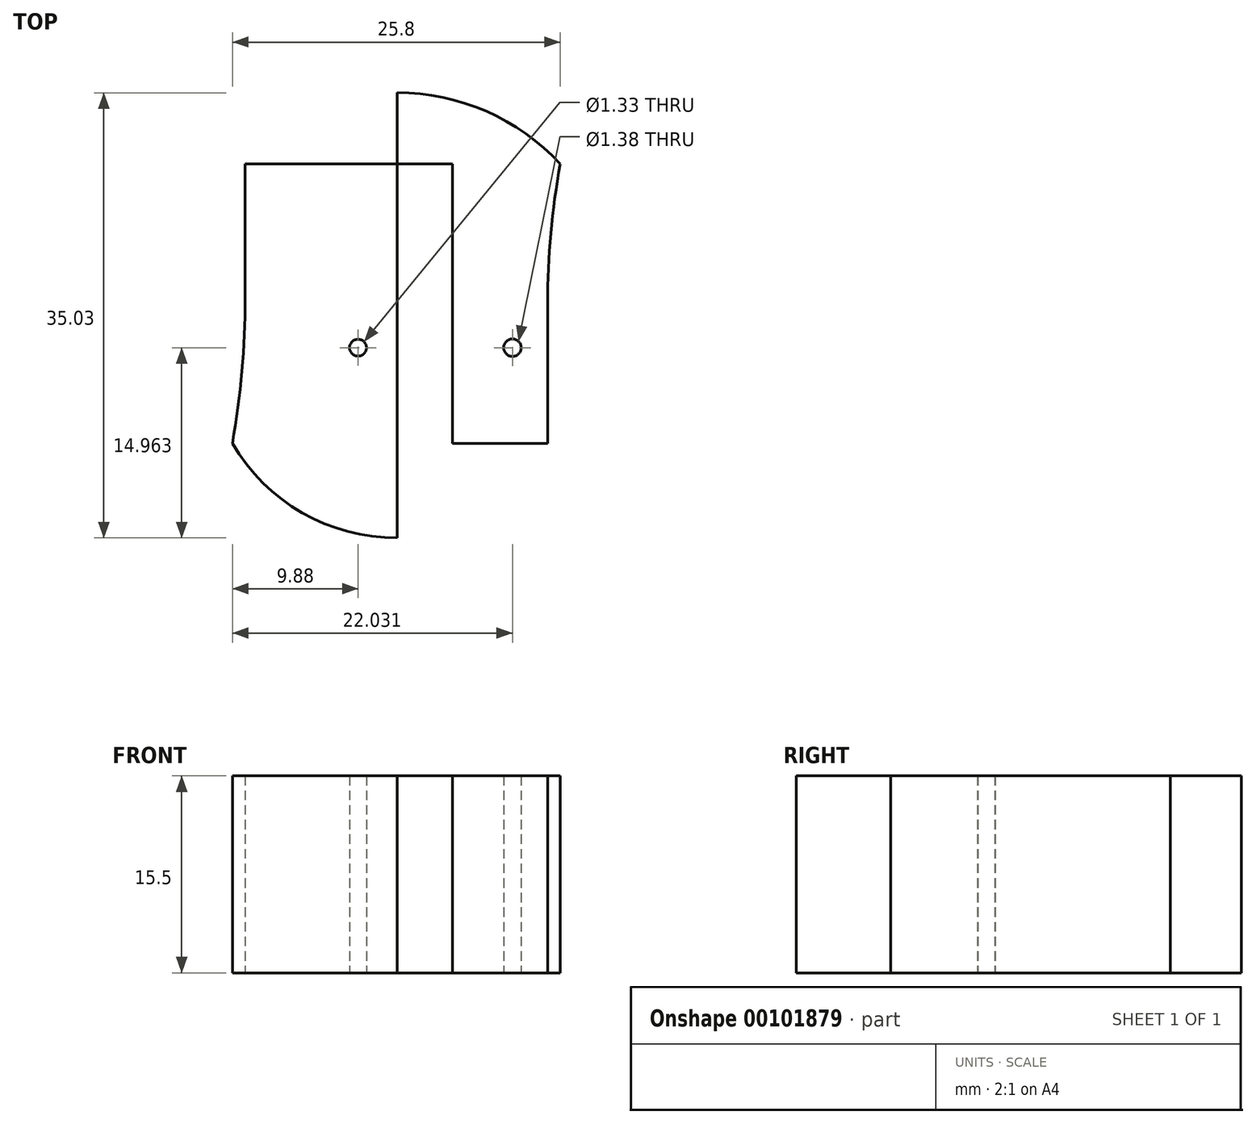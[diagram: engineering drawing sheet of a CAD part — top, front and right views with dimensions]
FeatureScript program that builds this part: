
annotation { "Feature Type Name" : "Feature", "Feature Type Description" : "" }
export const myFeature = defineFeature(function(context is Context, id is Id, definition is map)
    precondition{}
    {
        {
            var Q0;
            Q0=qCreatedBy(makeId("Top.planeOp"),FACE);
            var sketch = newSketch(context, id + "F0", { "sketchPlane" : qUnion([Q0])});
            skLineSegment(sketch, "E0.bottom", {"start": v(-29.3, -33.43) * mm, "end": v(-5.5, -33.43) * mm});
            skLineSegment(sketch, "E0.top", {"start": v(-29.3, -55.43) * mm, "end": v(-5.5, -55.43) * mm});
            skLineSegment(sketch, "E0.left", {"start": v(-29.3, -33.43) * mm, "end": v(-29.3, -55.43) * mm});
            skLineSegment(sketch, "E0.right", {"start": v(-5.5, -33.43) * mm, "end": v(-5.5, -55.43) * mm});
            skLineSegment(sketch, "E1", {"start": v(-26.8, -33.43) * mm, "end": v(-26.8, -55.43) * mm});
            skLineSegment(sketch, "E2", {"start": v(-7, -33.43) * mm, "end": v(-7, -55.43) * mm});
            skLineSegment(sketch, "E3", {"start": v(-17.4, -33.43) * mm, "end": v(-17.4, -46.37) * mm});
            skLineSegment(sketch, "E4", {"start": v(-17.4, -46.37) * mm, "end": v(-14.51, -46.37) * mm});
            skLineSegment(sketch, "E5", {"start": v(-14.51, -46.37) * mm, "end": v(-14.51, -55.43) * mm});
            skLineSegment(sketch, "E6", {"start": v(-18.41, -33.43) * mm, "end": v(-18.41, -55.43) * mm});
            skCircle(sketch, "E7", {"center": v(-20.42, -47.9) * mm, "radius": 0.66 * mm});
            skCircle(sketch, "E8", {"center": v(-8.27, -47.9) * mm, "radius": 0.69 * mm});
            skLineSegment(sketch, "E9", {"start": v(-12.98, -55.43) * mm, "end": v(-12.98, -33.43) * mm});
            skArc(sketch, "E10", {"start": v(-30.3, -55.43) * mm, "mid": v(-17.4, -62.86) * mm, "end": v(-4.5, -55.43) * mm});
            skArc(sketch, "E11", {"start": v(-4.5, -33.43) * mm, "mid": v(-17.33, -27.83) * mm, "end": v(-30.17, -33.43) * mm});
            skArc(sketch, "E12", {"start": v(-30.3, -55.43) * mm, "mid": v(-29.3, -44.43) * mm, "end": v(-30.17, -33.43) * mm});
            skArc(sketch, "E13", {"start": v(-4.5, -33.43) * mm, "mid": v(-5.5, -44.43) * mm, "end": v(-4.5, -55.43) * mm});
            skLineSegment(sketch, "E14", {"start": v(-17.33, -27.83) * mm, "end": v(-17.33, -62.86) * mm});
            skSolve(sketch);
        }
        {
            var Q0;
            {var subQ1=sQuery(id+"F0.wireOp",EDGE,"E10");Q0=makeQuery(id+"F0.imprint","IMPRINT",FACE,{"disambiguationData":[TD([[makeQuery(id+"F0.imprint","IMPRINT",EDGE,{"derivedFrom":subQ1}),1.0]])]});}
            var Q1;
            {var subQ0=sQuery(id+"F0.wireOp",EDGE,"E11");Q1=makeQuery(id+"F0.imprint","IMPRINT",FACE,{"disambiguationData":[TD([[makeQuery(id+"F0.imprint","IMPRINT",EDGE,{"derivedFrom":subQ0}),1.0]])]});}
            var Q2;
            {var subQ4=sQuery(id+"F0.wireOp",EDGE,"E1");Q2=makeQuery(id+"F0.imprint","IMPRINT",FACE,{"disambiguationData":[TD([[makeQuery(id+"F0.imprint","IMPRINT",EDGE,{"derivedFrom":subQ4}),-1.0]])]});}
            var Q3;
            {var subQ1=sQuery(id+"F0.wireOp",EDGE,"E1");Q3=makeQuery(id+"F0.imprint","IMPRINT",FACE,{"disambiguationData":[TD([[makeQuery(id+"F0.imprint","IMPRINT",EDGE,{"derivedFrom":subQ1}),1.0]])]});}
            var Q4;
            {var subQ3=sQuery(id+"F0.wireOp",EDGE,"E3");Q4=makeQuery(id+"F0.imprint","IMPRINT",FACE,{"disambiguationData":[TD([[makeQuery(id+"F0.imprint","IMPRINT",EDGE,{"derivedFrom":subQ3}),-1.0]])]});}
            var Q5;
            {var subQ3=sQuery(id+"F0.wireOp",EDGE,"E3");Q5=makeQuery(id+"F0.imprint","IMPRINT",FACE,{"disambiguationData":[TD([[makeQuery(id+"F0.imprint","IMPRINT",EDGE,{"derivedFrom":subQ3}),1.0]])]});}
            var Q6;
            {var subQ0=sQuery(id+"F0.wireOp",EDGE,"E2");Q6=makeQuery(id+"F0.imprint","IMPRINT",FACE,{"disambiguationData":[TD([[makeQuery(id+"F0.imprint","IMPRINT",EDGE,{"derivedFrom":subQ0}),-1.0]])]});}
            var Q7;
            {var subQ6=sQuery(id+"F0.wireOp",EDGE,"E2");Q7=makeQuery(id+"F0.imprint","IMPRINT",FACE,{"disambiguationData":[TD([[makeQuery(id+"F0.imprint","IMPRINT",EDGE,{"derivedFrom":subQ6}),1.0]])]});}
            extrude(context, id + "F1", {"entities" : qUnion([Q0, Q1, Q2, Q3, Q4, Q5, Q6, Q7]), "depth" : 15.5 * mm});
        }
    });
